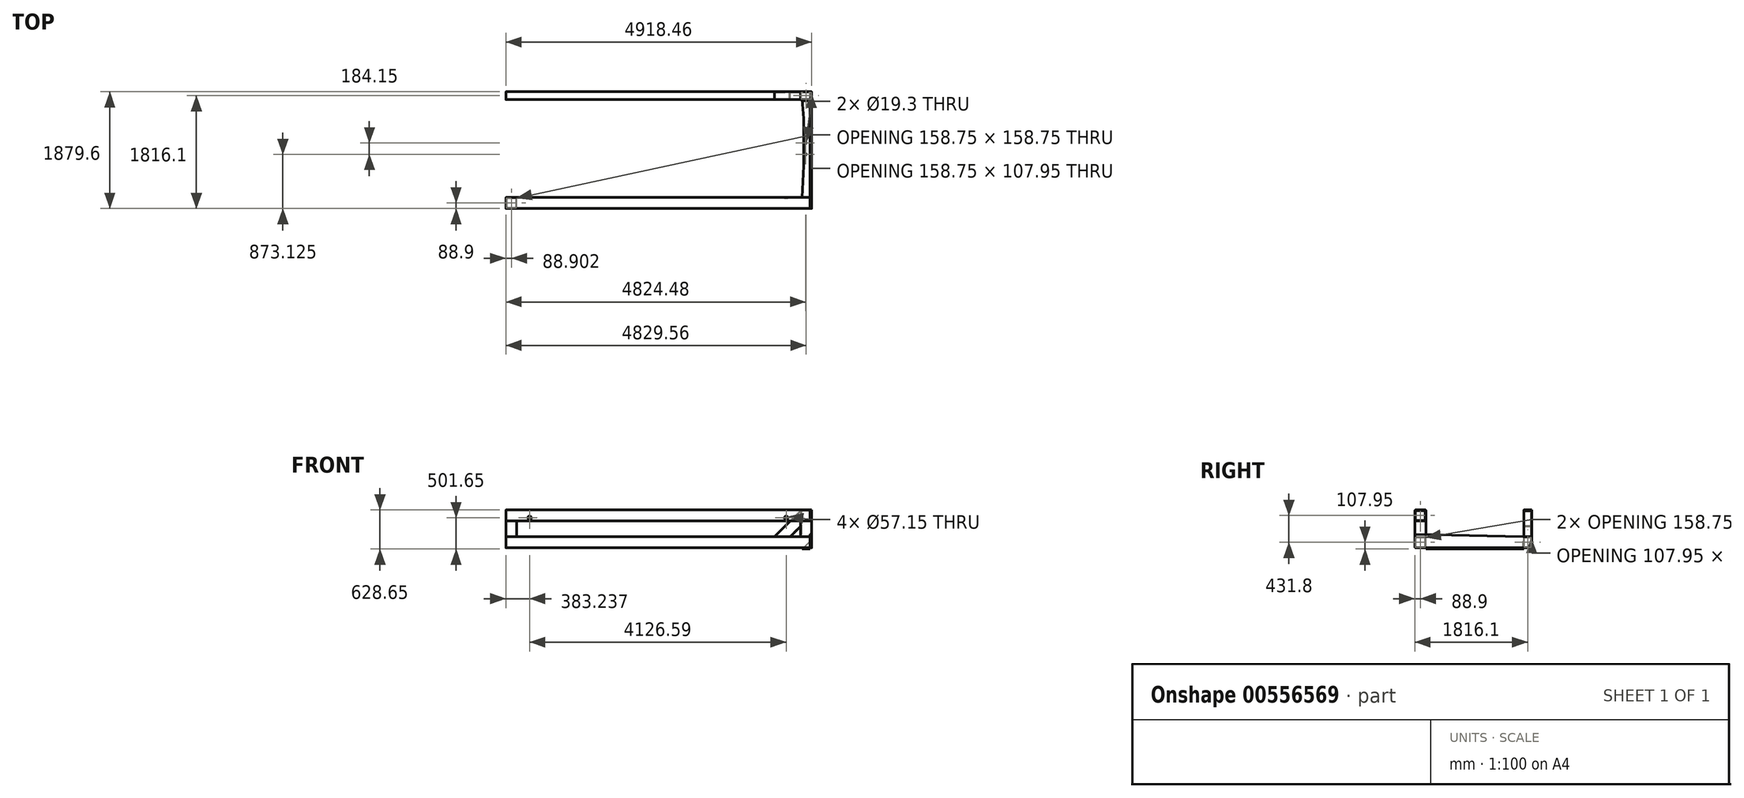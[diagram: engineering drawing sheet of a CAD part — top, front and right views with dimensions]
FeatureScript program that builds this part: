
annotation { "Feature Type Name" : "Feature", "Feature Type Description" : "" }
export const myFeature = defineFeature(function(context is Context, id is Id, definition is map)
    precondition{}
    {
        {
            var Q0;
            Q0=qCreatedBy(makeId("Right.planeOp"),FACE);
            var sketch = newSketch(context, id + "F0", { "sketchPlane" : qUnion([Q0])});
            skLineSegment(sketch, "E0.bottom", {"start": v(12.7, 0) * mm, "end": v(165.1, 0) * mm});
            skLineSegment(sketch, "E0.top", {"start": v(12.7, 177.8) * mm, "end": v(165.1, 177.8) * mm});
            skLineSegment(sketch, "E0.left", {"start": v(0, 12.7) * mm, "end": v(0, 165.1) * mm});
            skLineSegment(sketch, "E0.right", {"start": v(177.8, 12.7) * mm, "end": v(177.8, 165.1) * mm});
            skPoint(sketch, "E1.visualSharp", {"position": v(0, 177.8) * mm});
            skArc(sketch, "E1.filletArc", {"start": v(12.7, 177.8) * mm, "mid": v(3.72, 174.08) * mm, "end": v(0, 165.1) * mm});
            skPoint(sketch, "E2.visualSharp", {"position": v(177.8, 177.8) * mm});
            skArc(sketch, "E2.filletArc", {"start": v(177.8, 165.1) * mm, "mid": v(174.08, 174.08) * mm, "end": v(165.1, 177.8) * mm});
            skPoint(sketch, "E3.visualSharp", {"position": v(177.8, 0) * mm});
            skArc(sketch, "E3.filletArc", {"start": v(165.1, 0) * mm, "mid": v(174.08, 3.72) * mm, "end": v(177.8, 12.7) * mm});
            skPoint(sketch, "E4.visualSharp", {"position": v(0, 0) * mm});
            skArc(sketch, "E4.filletArc", {"start": v(0, 12.7) * mm, "mid": v(3.72, 3.72) * mm, "end": v(12.7, 0) * mm});
            skLineSegment(sketch, "E5.0", {"start": v(12.7, 168.28) * mm, "end": v(165.1, 168.28) * mm});
            skArc(sketch, "E5.1", {"start": v(168.28, 165.1) * mm, "mid": v(167.35, 167.35) * mm, "end": v(165.1, 168.28) * mm});
            skArc(sketch, "E5.2", {"start": v(12.7, 168.28) * mm, "mid": v(10.45, 167.35) * mm, "end": v(9.52, 165.1) * mm});
            skLineSegment(sketch, "E5.3", {"start": v(168.28, 12.7) * mm, "end": v(168.27, 165.1) * mm});
            skLineSegment(sketch, "E5.4", {"start": v(9.53, 12.7) * mm, "end": v(9.52, 165.1) * mm});
            skArc(sketch, "E5.5", {"start": v(9.53, 12.7) * mm, "mid": v(10.45, 10.45) * mm, "end": v(12.7, 9.53) * mm});
            skLineSegment(sketch, "E5.6", {"start": v(12.7, 9.53) * mm, "end": v(165.1, 9.53) * mm});
            skArc(sketch, "E5.7", {"start": v(165.1, 9.53) * mm, "mid": v(167.35, 10.45) * mm, "end": v(168.28, 12.7) * mm});
            skSolve(sketch);
        }
        {
            var Q0;
            Q0 = qSketchRegion(id + "F0", true);
            extrude(context, id + "F1", {"entities" : qUnion([Q0]), "endBound" : BoundingType.SYMMETRIC, "depth" : 4893.06 * mm, "offsetDistance" : 25.4 * mm});
        }
        {
            var Q0;
            Q0=makeQuery(id+"F1.opExtrude","SWEPT_FACE",FACE,{"disambiguationData":[OSD([sQuery(id+"F0.wireOp",EDGE,"E0.top")])]});
            var sketch = newSketch(context, id + "F2", { "sketchPlane" : qUnion([Q0])});
            skLineSegment(sketch, "E6.bottom", {"start": v(-2433.83, 0) * mm, "end": v(-2281.43, 0) * mm});
            skLineSegment(sketch, "E6.top", {"start": v(-2433.83, 177.8) * mm, "end": v(-2281.43, 177.8) * mm});
            skLineSegment(sketch, "E6.left", {"start": v(-2446.53, 12.7) * mm, "end": v(-2446.53, 165.1) * mm});
            skLineSegment(sketch, "E6.right", {"start": v(-2268.73, 12.7) * mm, "end": v(-2268.73, 165.1) * mm});
            skPoint(sketch, "E7.visualSharp", {"position": v(-2446.53, 177.8) * mm});
            skArc(sketch, "E7.filletArc", {"start": v(-2433.83, 177.8) * mm, "mid": v(-2442.8, 174.08) * mm, "end": v(-2446.53, 165.1) * mm});
            skPoint(sketch, "E8.visualSharp", {"position": v(-2268.73, 177.8) * mm});
            skArc(sketch, "E8.filletArc", {"start": v(-2268.73, 165.1) * mm, "mid": v(-2272.45, 174.08) * mm, "end": v(-2281.43, 177.8) * mm});
            skPoint(sketch, "E9.visualSharp", {"position": v(-2268.73, 0) * mm});
            skArc(sketch, "E9.filletArc", {"start": v(-2281.43, 0) * mm, "mid": v(-2272.45, 3.72) * mm, "end": v(-2268.73, 12.7) * mm});
            skPoint(sketch, "E10.visualSharp", {"position": v(-2446.53, 0) * mm});
            skArc(sketch, "E10.filletArc", {"start": v(-2446.53, 12.7) * mm, "mid": v(-2442.8, 3.72) * mm, "end": v(-2433.83, 0) * mm});
            skLineSegment(sketch, "E11.0", {"start": v(-2433.83, 168.28) * mm, "end": v(-2281.43, 168.28) * mm});
            skArc(sketch, "E11.1", {"start": v(-2278.25, 165.1) * mm, "mid": v(-2279.18, 167.35) * mm, "end": v(-2281.43, 168.28) * mm});
            skArc(sketch, "E11.2", {"start": v(-2433.83, 168.28) * mm, "mid": v(-2436.07, 167.35) * mm, "end": v(-2437, 165.1) * mm});
            skLineSegment(sketch, "E11.3", {"start": v(-2278.25, 12.7) * mm, "end": v(-2278.25, 165.1) * mm});
            skLineSegment(sketch, "E11.4", {"start": v(-2437, 12.7) * mm, "end": v(-2437, 165.1) * mm});
            skArc(sketch, "E11.5", {"start": v(-2437, 12.7) * mm, "mid": v(-2436.07, 10.45) * mm, "end": v(-2433.83, 9.53) * mm});
            skLineSegment(sketch, "E11.6", {"start": v(-2433.83, 9.53) * mm, "end": v(-2281.43, 9.53) * mm});
            skArc(sketch, "E11.7", {"start": v(-2281.43, 9.53) * mm, "mid": v(-2279.18, 10.45) * mm, "end": v(-2278.25, 12.7) * mm});
            skSolve(sketch);
        }
        {
            var Q0;
            Q0 = qSketchRegion(id + "F2", true);
            extrude(context, id + "F3", {"entities" : qUnion([Q0]), "depth" : 254 * mm, "offsetDistance" : 25.4 * mm});
        }
        {
            var Q0;
            Q0=qCreatedBy(makeId("Right.planeOp"),FACE);
            var sketch = newSketch(context, id + "F4", { "sketchPlane" : qUnion([Q0])});
            skLineSegment(sketch, "E12.bottom", {"start": v(12.7, 431.8) * mm, "end": v(165.1, 431.8) * mm});
            skLineSegment(sketch, "E12.top", {"start": v(12.7, 609.6) * mm, "end": v(165.1, 609.6) * mm});
            skLineSegment(sketch, "E12.left", {"start": v(0, 444.5) * mm, "end": v(0, 596.9) * mm});
            skLineSegment(sketch, "E12.right", {"start": v(177.8, 444.5) * mm, "end": v(177.8, 596.9) * mm});
            skPoint(sketch, "E13.visualSharp", {"position": v(0, 609.6) * mm});
            skArc(sketch, "E13.filletArc", {"start": v(12.7, 609.6) * mm, "mid": v(3.72, 605.88) * mm, "end": v(0, 596.9) * mm});
            skPoint(sketch, "E14.visualSharp", {"position": v(177.8, 609.6) * mm});
            skArc(sketch, "E14.filletArc", {"start": v(177.8, 596.9) * mm, "mid": v(174.08, 605.88) * mm, "end": v(165.1, 609.6) * mm});
            skPoint(sketch, "E15.visualSharp", {"position": v(177.8, 431.8) * mm});
            skArc(sketch, "E15.filletArc", {"start": v(165.1, 431.8) * mm, "mid": v(174.08, 435.52) * mm, "end": v(177.8, 444.5) * mm});
            skPoint(sketch, "E16.visualSharp", {"position": v(0, 431.8) * mm});
            skArc(sketch, "E16.filletArc", {"start": v(0, 444.5) * mm, "mid": v(3.72, 435.52) * mm, "end": v(12.7, 431.8) * mm});
            skLineSegment(sketch, "E17.0", {"start": v(12.7, 600.08) * mm, "end": v(165.1, 600.08) * mm});
            skArc(sketch, "E17.1", {"start": v(168.27, 596.9) * mm, "mid": v(167.35, 599.15) * mm, "end": v(165.1, 600.08) * mm});
            skArc(sketch, "E17.2", {"start": v(12.7, 600.08) * mm, "mid": v(10.45, 599.15) * mm, "end": v(9.52, 596.9) * mm});
            skLineSegment(sketch, "E17.3", {"start": v(168.28, 444.5) * mm, "end": v(168.27, 596.9) * mm});
            skLineSegment(sketch, "E17.4", {"start": v(9.53, 444.5) * mm, "end": v(9.52, 596.9) * mm});
            skArc(sketch, "E17.5", {"start": v(9.53, 444.5) * mm, "mid": v(10.45, 442.25) * mm, "end": v(12.7, 441.33) * mm});
            skLineSegment(sketch, "E17.6", {"start": v(12.7, 441.33) * mm, "end": v(165.1, 441.33) * mm});
            skArc(sketch, "E17.7", {"start": v(165.1, 441.33) * mm, "mid": v(167.35, 442.25) * mm, "end": v(168.28, 444.5) * mm});
            skSolve(sketch);
        }
        {
            var Q0;
            Q0 = qSketchRegion(id + "F4", true);
            extrude(context, id + "F5", {"entities" : qUnion([Q0]), "endBound" : BoundingType.SYMMETRIC, "depth" : 4893.06 * mm, "offsetDistance" : 25.4 * mm});
        }
        {
            var Q0;
            Q0=makeQuery(id+"F1.opExtrude","CAP_FACE",FACE,{"disambiguationData":[OSD([sQuery(id+"F0.wireOp",EDGE,"E0.bottom"),sQuery(id+"F0.wireOp",EDGE,"E0.top"),sQuery(id+"F0.wireOp",EDGE,"E0.left"),sQuery(id+"F0.wireOp",EDGE,"E0.right"),sQuery(id+"F0.wireOp",EDGE,"E1.filletArc"),sQuery(id+"F0.wireOp",EDGE,"E2.filletArc"),sQuery(id+"F0.wireOp",EDGE,"E3.filletArc"),sQuery(id+"F0.wireOp",EDGE,"E4.filletArc"),sQuery(id+"F0.wireOp",EDGE,"E5.0"),sQuery(id+"F0.wireOp",EDGE,"E5.1"),sQuery(id+"F0.wireOp",EDGE,"E5.2"),sQuery(id+"F0.wireOp",EDGE,"E5.3"),sQuery(id+"F0.wireOp",EDGE,"E5.4"),sQuery(id+"F0.wireOp",EDGE,"E5.5"),sQuery(id+"F0.wireOp",EDGE,"E5.6"),sQuery(id+"F0.wireOp",EDGE,"E5.7")])],"isStart":false});
            var sketch = newSketch(context, id + "F6", { "sketchPlane" : qUnion([Q0])});
            skLineSegment(sketch, "E18.bottom", {"start": v(12.7, 0) * mm, "end": v(1866.9, 0) * mm});
            skLineSegment(sketch, "E18.left", {"start": v(0, 12.7) * mm, "end": v(0, 203.2) * mm});
            skLineSegment(sketch, "E18.right", {"start": v(1879.6, 12.7) * mm, "end": v(1879.6, 165.1) * mm});
            skArc(sketch, "E19.0", {"start": v(0, 12.7) * mm, "mid": v(3.72, 3.72) * mm, "end": v(12.7, 0) * mm});
            skArc(sketch, "E20.filletArc", {"start": v(12.98, 215.9) * mm, "mid": v(3.82, 212.28) * mm, "end": v(0, 203.2) * mm});
            skArc(sketch, "E21.filletArc", {"start": v(1879.6, 165.1) * mm, "mid": v(1875.88, 174.08) * mm, "end": v(1866.9, 177.8) * mm});
            skArc(sketch, "E22.filletArc", {"start": v(1866.9, 0) * mm, "mid": v(1875.88, 3.72) * mm, "end": v(1879.6, 12.7) * mm});
            skLineSegment(sketch, "E23", {"start": v(1866.9, 177.8) * mm, "end": v(1739.9, 177.8) * mm});
            skLineSegment(sketch, "E24", {"start": v(1739.9, 177.8) * mm, "end": v(12.98, 215.9) * mm});
            skSolve(sketch);
        }
        {
            var Q0;
            Q0 = qSketchRegion(id + "F6", true);
            extrude(context, id + "F7", {"entities" : qUnion([Q0]), "depth" : 25.4 * mm, "offsetDistance" : 25.4 * mm});
        }
        {
            var Q0;
            Q0=qCreatedBy(makeId("Right.planeOp"),FACE);
            var sketch = newSketch(context, id + "F8", { "sketchPlane" : qUnion([Q0])});
            skLineSegment(sketch, "E25.bottom", {"start": v(1765.3, 0) * mm, "end": v(1866.9, 0) * mm});
            skLineSegment(sketch, "E25.top", {"start": v(1765.3, 177.8) * mm, "end": v(1866.9, 177.8) * mm});
            skLineSegment(sketch, "E25.left", {"start": v(1752.6, 12.7) * mm, "end": v(1752.6, 165.1) * mm});
            skLineSegment(sketch, "E25.right", {"start": v(1879.6, 12.7) * mm, "end": v(1879.6, 165.1) * mm});
            skPoint(sketch, "E26.visualSharp", {"position": v(1752.6, 177.8) * mm});
            skArc(sketch, "E26.filletArc", {"start": v(1765.3, 177.8) * mm, "mid": v(1756.32, 174.08) * mm, "end": v(1752.6, 165.1) * mm});
            skPoint(sketch, "E27.visualSharp", {"position": v(1879.6, 177.8) * mm});
            skArc(sketch, "E27.filletArc", {"start": v(1879.6, 165.1) * mm, "mid": v(1875.88, 174.08) * mm, "end": v(1866.9, 177.8) * mm});
            skPoint(sketch, "E28.visualSharp", {"position": v(1879.6, 0) * mm});
            skArc(sketch, "E28.filletArc", {"start": v(1866.9, 0) * mm, "mid": v(1875.88, 3.72) * mm, "end": v(1879.6, 12.7) * mm});
            skPoint(sketch, "E29.visualSharp", {"position": v(1752.6, 0) * mm});
            skArc(sketch, "E29.filletArc", {"start": v(1752.6, 12.7) * mm, "mid": v(1756.32, 3.72) * mm, "end": v(1765.3, 0) * mm});
            skLineSegment(sketch, "E30.0", {"start": v(1765.3, 168.28) * mm, "end": v(1866.9, 168.28) * mm});
            skArc(sketch, "E30.1", {"start": v(1870.08, 165.1) * mm, "mid": v(1869.15, 167.35) * mm, "end": v(1866.9, 168.28) * mm});
            skArc(sketch, "E30.2", {"start": v(1765.3, 168.28) * mm, "mid": v(1763.05, 167.35) * mm, "end": v(1762.13, 165.1) * mm});
            skLineSegment(sketch, "E30.3", {"start": v(1870.08, 12.7) * mm, "end": v(1870.08, 165.1) * mm});
            skLineSegment(sketch, "E30.4", {"start": v(1762.13, 12.7) * mm, "end": v(1762.13, 165.1) * mm});
            skArc(sketch, "E30.5", {"start": v(1762.13, 12.7) * mm, "mid": v(1763.05, 10.45) * mm, "end": v(1765.3, 9.53) * mm});
            skLineSegment(sketch, "E30.6", {"start": v(1765.3, 9.53) * mm, "end": v(1866.9, 9.53) * mm});
            skArc(sketch, "E30.7", {"start": v(1866.9, 9.53) * mm, "mid": v(1869.15, 10.45) * mm, "end": v(1870.08, 12.7) * mm});
            skSolve(sketch);
        }
        {
            var Q0;
            Q0 = qSketchRegion(id + "F8", true);
            extrude(context, id + "F9", {"entities" : qUnion([Q0]), "endBound" : BoundingType.SYMMETRIC, "depth" : 4893.06 * mm, "offsetDistance" : 25.4 * mm});
        }
        {
            var Q0;
            Q0=makeQuery(id+"F9.opExtrude","SWEPT_FACE",FACE,{"disambiguationData":[OSD([sQuery(id+"F8.wireOp",EDGE,"E25.top")])]});
            var sketch = newSketch(context, id + "F10", { "sketchPlane" : qUnion([Q0])});
            skLineSegment(sketch, "E31.bottom", {"start": v(2306.83, 1752.6) * mm, "end": v(2459.23, 1752.6) * mm});
            skLineSegment(sketch, "E31.top", {"start": v(2306.83, 1879.6) * mm, "end": v(2459.23, 1879.6) * mm});
            skLineSegment(sketch, "E31.left", {"start": v(2294.13, 1765.3) * mm, "end": v(2294.13, 1866.9) * mm});
            skLineSegment(sketch, "E31.right", {"start": v(2471.93, 1765.3) * mm, "end": v(2471.93, 1866.9) * mm});
            skPoint(sketch, "E32.visualSharp", {"position": v(2294.13, 1879.6) * mm});
            skArc(sketch, "E32.filletArc", {"start": v(2306.83, 1879.6) * mm, "mid": v(2297.85, 1875.88) * mm, "end": v(2294.13, 1866.9) * mm});
            skPoint(sketch, "E33.visualSharp", {"position": v(2471.93, 1879.6) * mm});
            skArc(sketch, "E33.filletArc", {"start": v(2471.93, 1866.9) * mm, "mid": v(2468.2, 1875.88) * mm, "end": v(2459.23, 1879.6) * mm});
            skPoint(sketch, "E34.visualSharp", {"position": v(2471.93, 1752.6) * mm});
            skArc(sketch, "E34.filletArc", {"start": v(2459.23, 1752.6) * mm, "mid": v(2468.2, 1756.32) * mm, "end": v(2471.93, 1765.3) * mm});
            skPoint(sketch, "E35.visualSharp", {"position": v(2294.13, 1752.6) * mm});
            skArc(sketch, "E35.filletArc", {"start": v(2294.13, 1765.3) * mm, "mid": v(2297.85, 1756.32) * mm, "end": v(2306.83, 1752.6) * mm});
            skLineSegment(sketch, "E36.0", {"start": v(2306.83, 1870.08) * mm, "end": v(2459.23, 1870.08) * mm});
            skArc(sketch, "E36.1", {"start": v(2462.4, 1866.9) * mm, "mid": v(2461.47, 1869.15) * mm, "end": v(2459.23, 1870.08) * mm});
            skArc(sketch, "E36.2", {"start": v(2306.83, 1870.08) * mm, "mid": v(2304.58, 1869.15) * mm, "end": v(2303.65, 1866.9) * mm});
            skLineSegment(sketch, "E36.3", {"start": v(2462.4, 1765.3) * mm, "end": v(2462.4, 1866.9) * mm});
            skLineSegment(sketch, "E36.4", {"start": v(2303.65, 1765.3) * mm, "end": v(2303.65, 1866.9) * mm});
            skArc(sketch, "E36.5", {"start": v(2303.65, 1765.3) * mm, "mid": v(2304.58, 1763.05) * mm, "end": v(2306.83, 1762.13) * mm});
            skLineSegment(sketch, "E36.6", {"start": v(2306.83, 1762.13) * mm, "end": v(2459.23, 1762.13) * mm});
            skArc(sketch, "E36.7", {"start": v(2459.23, 1762.13) * mm, "mid": v(2461.47, 1763.05) * mm, "end": v(2462.4, 1765.3) * mm});
            skSolve(sketch);
        }
        {
            var Q0;
            Q0 = qSketchRegion(id + "F10", true);
            extrude(context, id + "F11", {"entities" : qUnion([Q0]), "depth" : 419.1 * mm, "offsetDistance" : 25.4 * mm});
        }
        {
            var Q0;
            Q0=makeQuery(id+"F9.opExtrude","SWEPT_FACE",FACE,{"disambiguationData":[OSD([sQuery(id+"F8.wireOp",EDGE,"E25.right")])]});
            var sketch = newSketch(context, id + "F12", { "sketchPlane" : qUnion([Q0])});
            skLineSegment(sketch, "E37", {"start": v(-2294.13, 596.9) * mm, "end": v(-1875.03, 177.8) * mm});
            skLineSegment(sketch, "E38", {"start": v(-1875.03, 177.8) * mm, "end": v(-2126.48, 177.8) * mm});
            skLineSegment(sketch, "E39", {"start": v(-2126.48, 177.8) * mm, "end": v(-2294.13, 345.45) * mm});
            skLineSegment(sketch, "E40", {"start": v(-2294.13, 345.45) * mm, "end": v(-2294.13, 596.9) * mm});
            skSolve(sketch);
        }
        {
            var Q0;
            Q0 = qSketchRegion(id + "F12", true);
            var Q1;
            Q1=makeQuery(id+"F11.opExtrude","SWEPT_FACE",FACE,{"disambiguationData":[OSD([sQuery(id+"F10.wireOp",EDGE,"E31.bottom")])]});
            extrude(context, id + "F13", {"entities" : qUnion([Q0]), "endBound" : BoundingType.UP_TO_SURFACE, "oppositeDirection" : true, "depth" : 25.4 * mm, "endBoundEntityFace" : qUnion([Q1]), "offsetDistance" : 25.4 * mm});
        }
        {
            var Q0;
            Q0=makeQuery(id+"F13.opExtrude","CAP_EDGE",EDGE,{"disambiguationData":[OSD([sQuery(id+"F12.wireOp",EDGE,"E37")])],"isStart":true});
            var Q1;
            Q1=makeQuery(id+"F13.opExtrude","CAP_EDGE",EDGE,{"disambiguationData":[OSD([sQuery(id+"F12.wireOp",EDGE,"E39")])],"isStart":true});
            var Q2;
            Q2=makeQuery(id+"F13.opExtrude","TWEAK_EDGE",EDGE,{"derivedFrom":[makeQuery(id+"F11.opExtrude","SWEPT_FACE",FACE,{"disambiguationData":[OSD([sQuery(id+"F10.wireOp",EDGE,"E31.bottom")])]}),makeQuery(id+"F12.imprint","IMPRINT",EDGE,{"derivedFrom":sQuery(id+"F12.wireOp",EDGE,"E37")})]});
            var Q3;
            Q3=makeQuery(id+"F13.opExtrude","TWEAK_EDGE",EDGE,{"derivedFrom":[makeQuery(id+"F11.opExtrude","SWEPT_FACE",FACE,{"disambiguationData":[OSD([sQuery(id+"F10.wireOp",EDGE,"E31.bottom")])]}),makeQuery(id+"F12.imprint","IMPRINT",EDGE,{"derivedFrom":sQuery(id+"F12.wireOp",EDGE,"E39")})]});
            fillet(context, id + "F14", {"entities" : qUnion([Q0, Q1, Q2, Q3]), "radius" : 12.7 * mm, "tangentPropagation" : true, "allowEdgeOverflow" : false});
        }
        {
            var Q0;
            Q0=makeQuery(id+"F13.opExtrude","SWEPT_FACE",FACE,{"disambiguationData":[OSD([sQuery(id+"F12.wireOp",EDGE,"E40")])]});
            var Q1;
            Q1=makeQuery(id+"F13.opExtrude","SWEPT_FACE",FACE,{"disambiguationData":[OSD([sQuery(id+"F12.wireOp",EDGE,"E38")])]});
            shell(context, id + "F15", {"entities" : qUnion([Q0, Q1]), "thickness" : 9.52 * mm});
        }
        {
            var Q0;
            Q0=makeQuery(id+"F11.opExtrude","CAP_FACE",FACE,{"disambiguationData":[OSD([sQuery(id+"F10.wireOp",EDGE,"E31.bottom"),sQuery(id+"F10.wireOp",EDGE,"E31.top"),sQuery(id+"F10.wireOp",EDGE,"E31.left"),sQuery(id+"F10.wireOp",EDGE,"E31.right"),sQuery(id+"F10.wireOp",EDGE,"E32.filletArc"),sQuery(id+"F10.wireOp",EDGE,"E33.filletArc"),sQuery(id+"F10.wireOp",EDGE,"E34.filletArc"),sQuery(id+"F10.wireOp",EDGE,"E35.filletArc"),sQuery(id+"F10.wireOp",EDGE,"E36.0"),sQuery(id+"F10.wireOp",EDGE,"E36.1"),sQuery(id+"F10.wireOp",EDGE,"E36.2"),sQuery(id+"F10.wireOp",EDGE,"E36.3"),sQuery(id+"F10.wireOp",EDGE,"E36.4"),sQuery(id+"F10.wireOp",EDGE,"E36.5"),sQuery(id+"F10.wireOp",EDGE,"E36.6"),sQuery(id+"F10.wireOp",EDGE,"E36.7")])],"isStart":false});
            var sketch = newSketch(context, id + "F16", { "sketchPlane" : qUnion([Q0])});
            skLineSegment(sketch, "E41.0", {"start": v(2306.83, 1752.6) * mm, "end": v(2459.23, 1752.6) * mm});
            skArc(sketch, "E41.1", {"start": v(2459.23, 1752.6) * mm, "mid": v(2468.2, 1756.32) * mm, "end": v(2471.93, 1765.3) * mm});
            skLineSegment(sketch, "E41.2", {"start": v(2471.93, 1765.3) * mm, "end": v(2471.93, 1866.9) * mm});
            skArc(sketch, "E41.3", {"start": v(2294.13, 1765.3) * mm, "mid": v(2297.85, 1756.32) * mm, "end": v(2306.83, 1752.6) * mm});
            skLineSegment(sketch, "E41.4", {"start": v(2294.13, 1765.3) * mm, "end": v(2294.13, 1866.9) * mm});
            skArc(sketch, "E41.5", {"start": v(2306.83, 1879.6) * mm, "mid": v(2297.85, 1875.88) * mm, "end": v(2294.13, 1866.9) * mm});
            skLineSegment(sketch, "E41.6", {"start": v(2306.83, 1879.6) * mm, "end": v(2459.23, 1879.6) * mm});
            skArc(sketch, "E41.7", {"start": v(2471.93, 1866.9) * mm, "mid": v(2468.2, 1875.88) * mm, "end": v(2459.23, 1879.6) * mm});
            skSolve(sketch);
        }
        {
            var Q0;
            Q0 = qSketchRegion(id + "F16", true);
            extrude(context, id + "F17", {"entities" : qUnion([Q0]), "depth" : 12.7 * mm, "offsetDistance" : 25.4 * mm});
        }
        {
            var Q0;
            Q0=makeQuery(id+"F5.opExtrude","CAP_FACE",FACE,{"disambiguationData":[OSD([sQuery(id+"F4.wireOp",EDGE,"E12.bottom"),sQuery(id+"F4.wireOp",EDGE,"E12.top"),sQuery(id+"F4.wireOp",EDGE,"E12.left"),sQuery(id+"F4.wireOp",EDGE,"E12.right"),sQuery(id+"F4.wireOp",EDGE,"E13.filletArc"),sQuery(id+"F4.wireOp",EDGE,"E14.filletArc"),sQuery(id+"F4.wireOp",EDGE,"E15.filletArc"),sQuery(id+"F4.wireOp",EDGE,"E16.filletArc"),sQuery(id+"F4.wireOp",EDGE,"E17.0"),sQuery(id+"F4.wireOp",EDGE,"E17.1"),sQuery(id+"F4.wireOp",EDGE,"E17.2"),sQuery(id+"F4.wireOp",EDGE,"E17.3"),sQuery(id+"F4.wireOp",EDGE,"E17.4"),sQuery(id+"F4.wireOp",EDGE,"E17.5"),sQuery(id+"F4.wireOp",EDGE,"E17.6"),sQuery(id+"F4.wireOp",EDGE,"E17.7")])],"isStart":false});
            var sketch = newSketch(context, id + "F18", { "sketchPlane" : qUnion([Q0])});
            skLineSegment(sketch, "E42.0", {"start": v(12.7, 600.08) * mm, "end": v(165.1, 600.08) * mm});
            skArc(sketch, "E42.1", {"start": v(12.7, 600.08) * mm, "mid": v(10.45, 599.15) * mm, "end": v(9.52, 596.9) * mm});
            skLineSegment(sketch, "E42.2", {"start": v(9.53, 444.5) * mm, "end": v(9.52, 596.9) * mm});
            skArc(sketch, "E42.3", {"start": v(9.53, 444.5) * mm, "mid": v(10.45, 442.25) * mm, "end": v(12.7, 441.33) * mm});
            skLineSegment(sketch, "E42.4", {"start": v(12.7, 441.33) * mm, "end": v(165.1, 441.33) * mm});
            skArc(sketch, "E42.5", {"start": v(165.1, 441.33) * mm, "mid": v(167.35, 442.25) * mm, "end": v(168.28, 444.5) * mm});
            skLineSegment(sketch, "E42.6", {"start": v(168.28, 444.5) * mm, "end": v(168.27, 596.9) * mm});
            skArc(sketch, "E42.7", {"start": v(168.27, 596.9) * mm, "mid": v(167.35, 599.15) * mm, "end": v(165.1, 600.08) * mm});
            skSolve(sketch);
        }
        {
            var Q0;
            Q0 = qSketchRegion(id + "F18", true);
            extrude(context, id + "F19", {"entities" : qUnion([Q0]), "depth" : 12.7 * mm, "offsetDistance" : 25.4 * mm});
        }
        {
            var Q0;
            Q0=makeQuery(id+"F1.opExtrude","SWEPT_FACE",FACE,{"disambiguationData":[OSD([sQuery(id+"F0.wireOp",EDGE,"E0.bottom")])]});
            var sketch = newSketch(context, id + "F20", { "sketchPlane" : qUnion([Q0])});
            skLineSegment(sketch, "E43", {"start": v(2446.53, -177.8) * mm, "end": v(2319.53, -177.8) * mm});
            skLineSegment(sketch, "E44", {"start": v(2319.53, -177.8) * mm, "end": v(2344.93, -685.8) * mm});
            skLineSegment(sketch, "E45", {"start": v(2344.93, -685.8) * mm, "end": v(2344.93, -1447.8) * mm});
            skLineSegment(sketch, "E46", {"start": v(2344.93, -1447.8) * mm, "end": v(2319.53, -1752.6) * mm});
            skLineSegment(sketch, "E47", {"start": v(2319.53, -1752.6) * mm, "end": v(2446.53, -1752.6) * mm});
            skLineSegment(sketch, "E48", {"start": v(2446.53, -1752.6) * mm, "end": v(2446.53, -177.8) * mm});
            skCircle(sketch, "E49", {"center": v(2377.95, -873.13) * mm, "radius": 9.65 * mm});
            skCircle(sketch, "E50", {"center": v(2377.95, -1057.28) * mm, "radius": 9.65 * mm});
            skLineSegment(sketch, "E51", {"start": v(2446.53, -965.2) * mm, "end": v(2344.93, -965.2) * mm, "construction": true});
            skSolve(sketch);
        }
        {
            var Q0;
            Q0 = qSketchRegion(id + "F20", true);
            extrude(context, id + "F21", {"entities" : qUnion([Q0]), "depth" : 19.05 * mm, "offsetDistance" : 25.4 * mm});
        }
        {
            var Q0;
            Q0=makeQuery(id+"F9.opExtrude","SWEPT_FACE",FACE,{"disambiguationData":[OSD([sQuery(id+"F8.wireOp",EDGE,"E25.left")])]});
            var sketch = newSketch(context, id + "F22", { "sketchPlane" : qUnion([Q0])});
            skLineSegment(sketch, "E52", {"start": v(2446.53, 101.6) * mm, "end": v(2446.53, 0) * mm});
            skLineSegment(sketch, "E53", {"start": v(2446.53, 0) * mm, "end": v(2344.93, 0) * mm});
            skLineSegment(sketch, "E54", {"start": v(2344.93, 0) * mm, "end": v(2446.53, 101.6) * mm});
            skSolve(sketch);
        }
        {
            var Q0;
            Q0 = qSketchRegion(id + "F22", true);
            extrude(context, id + "F23", {"entities" : qUnion([Q0]), "depth" : 19.05 * mm, "offsetDistance" : 25.4 * mm});
        }
        {
            var Q0;
            Q0=makeQuery(id+"F5.opExtrude","SWEPT_FACE",FACE,{"disambiguationData":[OSD([sQuery(id+"F4.wireOp",EDGE,"E12.left")])]});
            var sketch = newSketch(context, id + "F24", { "sketchPlane" : qUnion([Q0])});
            skCircle(sketch, "E55", {"center": v(-2063.3, 482.6) * mm, "radius": 28.58 * mm});
            skCircle(sketch, "E56", {"center": v(2063.3, 482.6) * mm, "radius": 28.58 * mm});
            skPoint(sketch, "E57", {"position": v(-2446.53, 520.7) * mm});
            skSolve(sketch);
        }
        {
            var Q0;
            Q0 = qSketchRegion(id + "F24", true);
            extrude(context, id + "F25", {"entities" : qUnion([Q0]), "operationType" : NewBodyOperationType.REMOVE, "endBound" : BoundingType.THROUGH_ALL, "oppositeDirection" : true, "depth" : 25.4 * mm, "offsetDistance" : 25.4 * mm});
        }
    });
